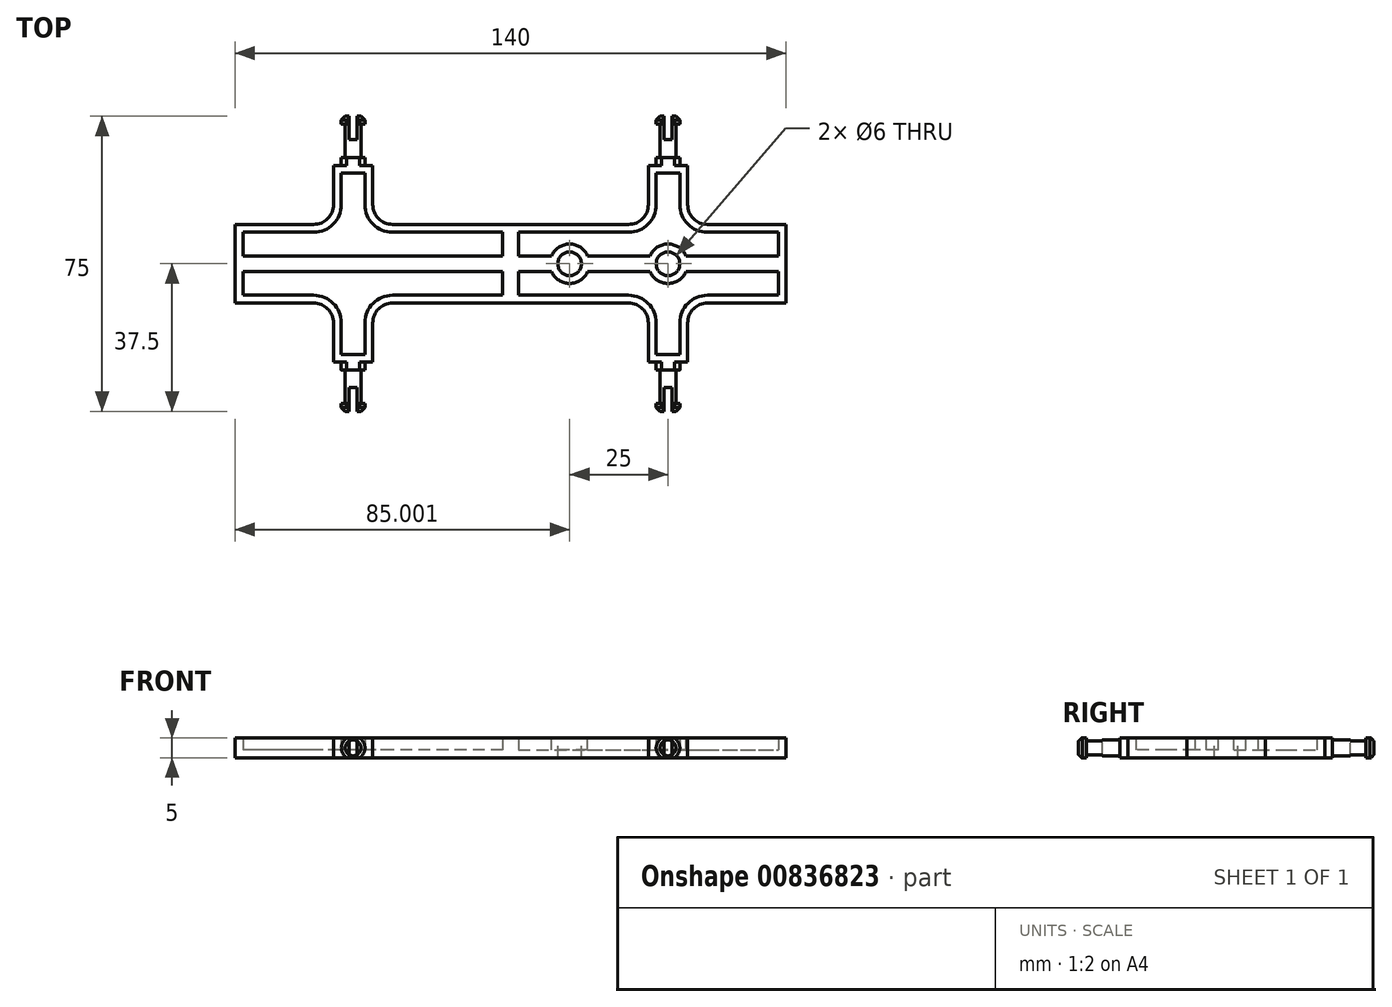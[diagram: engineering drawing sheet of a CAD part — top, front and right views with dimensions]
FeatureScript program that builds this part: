
annotation { "Feature Type Name" : "Feature", "Feature Type Description" : "" }
export const myFeature = defineFeature(function(context is Context, id is Id, definition is map)
    precondition{}
    {
        {
            var Q0;
            Q0=qCreatedBy(makeId("Front.planeOp"),FACE);
            var sketch = newSketch(context, id + "F0", { "sketchPlane" : qUnion([Q0])});
            skLineSegment(sketch, "E0.bottom", {"start": v(-42.85, 0) * mm, "end": v(27.15, 0) * mm});
            skLineSegment(sketch, "E0.top", {"start": v(-42.85, 10) * mm, "end": v(-12.85, 10) * mm});
            skLineSegment(sketch, "E0.left", {"start": v(-42.85, 0) * mm, "end": v(-42.85, 10) * mm});
            skLineSegment(sketch, "E0.right", {"start": v(27.15, 0) * mm, "end": v(27.15, 10) * mm});
            skLineSegment(sketch, "E1.top", {"start": v(-7.85, 25) * mm, "end": v(2.15, 25) * mm});
            skLineSegment(sketch, "E1.left", {"start": v(-7.85, 15) * mm, "end": v(-7.85, 25) * mm});
            skLineSegment(sketch, "E1.right", {"start": v(2.15, 15) * mm, "end": v(2.15, 25) * mm});
            skLineSegment(sketch, "E2.trimOffspring", {"start": v(7.15, 10) * mm, "end": v(27.15, 10) * mm});
            skPoint(sketch, "E3.visualSharp", {"position": v(-7.85, 10) * mm});
            skArc(sketch, "E3.filletArc", {"start": v(-12.85, 10) * mm, "mid": v(-9.31, 11.46) * mm, "end": v(-7.85, 15) * mm});
            skPoint(sketch, "E4.visualSharp", {"position": v(2.15, 10) * mm});
            skArc(sketch, "E4.filletArc", {"start": v(2.15, 15) * mm, "mid": v(3.62, 11.46) * mm, "end": v(7.15, 10) * mm});
            skSolve(sketch);
        }
        {
            var Q0;
            Q0=makeQuery(id+"F0.imprint","IMPRINT",FACE,{"disambiguationData":[TD([[makeQuery(id+"F0.imprint","IMPRINT",EDGE,{"derivedFrom":sQuery(id+"F0.wireOp",EDGE,"E0.bottom")}),1.0]])]});
            extrude(context, id + "F1", {"entities" : qUnion([Q0]), "endBound" : BoundingType.SYMMETRIC, "depth" : 5 * mm, "offsetDistance" : 25 * mm});
        }
        {
            var Q0;
            Q0=makeQuery(id+"F1.opExtrude","CAP_FACE",FACE,{"disambiguationData":[OSD([sQuery(id+"F0.wireOp",EDGE,"E0.bottom"),sQuery(id+"F0.wireOp",EDGE,"E0.top"),sQuery(id+"F0.wireOp",EDGE,"E0.left"),sQuery(id+"F0.wireOp",EDGE,"E0.right"),sQuery(id+"F0.wireOp",EDGE,"E1.top"),sQuery(id+"F0.wireOp",EDGE,"E1.left"),sQuery(id+"F0.wireOp",EDGE,"E1.right"),sQuery(id+"F0.wireOp",EDGE,"E2.trimOffspring"),sQuery(id+"F0.wireOp",EDGE,"E3.filletArc"),sQuery(id+"F0.wireOp",EDGE,"E4.filletArc")])],"isStart":false});
            shell(context, id + "F2", {"entities" : qUnion([Q0]), "thickness" : 2 * mm});
        }
        {
            var Q0;
            Q0=qCreatedBy(makeId("Front.planeOp"),FACE);
            var sketch = newSketch(context, id + "F3", { "sketchPlane" : qUnion([Q0])});
            skLineSegment(sketch, "E5", {"start": v(-5.85, 37.5) * mm, "end": v(-2.85, 37.5) * mm});
            skLineSegment(sketch, "E6", {"start": v(-2.85, 37.5) * mm, "end": v(-2.85, 25) * mm});
            skLineSegment(sketch, "E7", {"start": v(-2.85, 25) * mm, "end": v(-5.85, 25) * mm});
            skLineSegment(sketch, "E8", {"start": v(-5.85, 25) * mm, "end": v(-5.85, 27) * mm});
            skLineSegment(sketch, "E9", {"start": v(-5.85, 27) * mm, "end": v(-4.85, 27) * mm});
            skLineSegment(sketch, "E10", {"start": v(-4.85, 27) * mm, "end": v(-4.85, 35.5) * mm});
            skLineSegment(sketch, "E11", {"start": v(-4.85, 35.5) * mm, "end": v(-5.85, 35.5) * mm});
            skLineSegment(sketch, "E12", {"start": v(-5.85, 35.5) * mm, "end": v(-5.85, 37.5) * mm});
            skSolve(sketch);
        }
        {
            var Q0;
            Q0 = qSketchRegion(id + "F3", true);
            var Q1;
            Q1=sQuery(id+"F3.wireOp",EDGE,"E6");
            revolve(context, id + "F4", {"operationType" : NewBodyOperationType.ADD, "surfaceOperationType" : NewSurfaceOperationType.NEW, "entities" : qUnion([Q0]), "axis" : qUnion([Q1]), "revolveType" : RevolveType.FULL});
        }
        {
            var Q0;
            Q0=makeQuery(id+"F4.opRevolve","SWEPT_EDGE",EDGE,{"disambiguationData":[OSD([sQuery(id+"F3.wireOp",EDGE,"E5"),sQuery(id+"F3.wireOp",EDGE,"E12")])]});
            chamfer(context, id + "F5", {"entities" : qUnion([Q0]), "width" : 1 * mm, "tangentPropagation" : true});
        }
        {
            var Q0;
            Q0=makeQuery(id+"F4.opRevolve","SWEPT_FACE",FACE,{"disambiguationData":[OSD([sQuery(id+"F3.wireOp",EDGE,"E5")])]});
            var sketch = newSketch(context, id + "F6", { "sketchPlane" : qUnion([Q0])});
            skLineSegment(sketch, "E13.bottom", {"start": v(-55.26, 2.5) * mm, "end": v(46.37, 2.5) * mm});
            skLineSegment(sketch, "E13.top", {"start": v(-55.26, -2.5) * mm, "end": v(46.37, -2.5) * mm});
            skLineSegment(sketch, "E13.left", {"start": v(-55.26, 2.5) * mm, "end": v(-55.26, -2.5) * mm});
            skLineSegment(sketch, "E13.right", {"start": v(46.37, 2.5) * mm, "end": v(46.37, -2.5) * mm});
            skSolve(sketch);
        }
        {
            var Q0;
            Q0 = qSketchRegion(id + "F6", true);
            extrude(context, id + "F7", {"entities" : qUnion([Q0]), "operationType" : NewBodyOperationType.INTERSECT, "endBound" : BoundingType.THROUGH_ALL, "oppositeDirection" : true, "depth" : 25 * mm, "offsetDistance" : 25 * mm});
        }
        {
            var Q0;
            Q0=makeQuery(id+"F4.opRevolve","SWEPT_FACE",FACE,{"disambiguationData":[OSD([sQuery(id+"F3.wireOp",EDGE,"E5")])]});
            var sketch = newSketch(context, id + "F8", { "sketchPlane" : qUnion([Q0])});
            skLineSegment(sketch, "E14.bottom", {"start": v(-3.85, 6.1) * mm, "end": v(-1.85, 6.1) * mm});
            skLineSegment(sketch, "E14.top", {"start": v(-3.85, -6.84) * mm, "end": v(-1.85, -6.84) * mm});
            skLineSegment(sketch, "E14.left", {"start": v(-3.85, 6.1) * mm, "end": v(-3.85, -6.84) * mm});
            skLineSegment(sketch, "E14.right", {"start": v(-1.85, 6.1) * mm, "end": v(-1.85, -6.84) * mm});
            skSolve(sketch);
        }
        {
            var Q0;
            Q0 = qSketchRegion(id + "F8", true);
            extrude(context, id + "F9", {"entities" : qUnion([Q0]), "operationType" : NewBodyOperationType.REMOVE, "oppositeDirection" : true, "depth" : 6 * mm, "offsetDistance" : 25 * mm});
        }
        {
            var Q0;
            Q0=makeQuery(id+"F1.opExtrude","SWEPT_BODY",BODY,{"disambiguationData":[OSD([sQuery(id+"F0.wireOp",EDGE,"E0.bottom"),sQuery(id+"F0.wireOp",EDGE,"E0.top"),sQuery(id+"F0.wireOp",EDGE,"E0.left"),sQuery(id+"F0.wireOp",EDGE,"E0.right"),sQuery(id+"F0.wireOp",EDGE,"E1.top"),sQuery(id+"F0.wireOp",EDGE,"E1.left"),sQuery(id+"F0.wireOp",EDGE,"E1.right"),sQuery(id+"F0.wireOp",EDGE,"E2.trimOffspring"),sQuery(id+"F0.wireOp",EDGE,"E3.filletArc"),sQuery(id+"F0.wireOp",EDGE,"E4.filletArc")])]});
            var Q1;
            Q1=qCreatedBy(makeId("Top.planeOp"),FACE);
            mirror(context, id + "F10", {"operationType" : NewBodyOperationType.ADD, "entities" : qUnion([Q0]), "mirrorPlane" : qUnion([Q1])});
        }
        {
            var Q0;
            Q0=makeQuery(id+"F1.opExtrude","SWEPT_BODY",BODY,{"disambiguationData":[OSD([sQuery(id+"F0.wireOp",EDGE,"E0.bottom"),sQuery(id+"F0.wireOp",EDGE,"E0.top"),sQuery(id+"F0.wireOp",EDGE,"E0.left"),sQuery(id+"F0.wireOp",EDGE,"E0.right"),sQuery(id+"F0.wireOp",EDGE,"E1.top"),sQuery(id+"F0.wireOp",EDGE,"E1.left"),sQuery(id+"F0.wireOp",EDGE,"E1.right"),sQuery(id+"F0.wireOp",EDGE,"E2.trimOffspring"),sQuery(id+"F0.wireOp",EDGE,"E3.filletArc"),sQuery(id+"F0.wireOp",EDGE,"E4.filletArc")])]});
            var Q1;
            {var subQ0=makeQuery(id+"F1.opExtrude","SWEPT_FACE",FACE,{"disambiguationData":[OSD([sQuery(id+"F0.wireOp",EDGE,"E0.left")])]});Q1=makeQuery(id+"F10.boolean.opBoolean","MERGE",FACE,{"derivedFrom":[subQ0,makeQuery(id+"F10.opPattern","COPY",FACE,{"derivedFrom":subQ0,"instanceName":"1"})]});}
            mirror(context, id + "F11", {"operationType" : NewBodyOperationType.ADD, "entities" : qUnion([Q0]), "mirrorPlane" : qUnion([Q1])});
        }
        {
            var Q0;
            {var subQ0=makeQuery(id+"F7.boolean.opBoolean","MERGE",FACE,{"derivedFrom":[makeQuery(id+"F1.opExtrude","CAP_FACE",FACE,{"disambiguationData":[OSD([sQuery(id+"F0.wireOp",EDGE,"E0.bottom"),sQuery(id+"F0.wireOp",EDGE,"E0.top"),sQuery(id+"F0.wireOp",EDGE,"E0.left"),sQuery(id+"F0.wireOp",EDGE,"E0.right"),sQuery(id+"F0.wireOp",EDGE,"E1.top"),sQuery(id+"F0.wireOp",EDGE,"E1.left"),sQuery(id+"F0.wireOp",EDGE,"E1.right"),sQuery(id+"F0.wireOp",EDGE,"E2.trimOffspring"),sQuery(id+"F0.wireOp",EDGE,"E3.filletArc"),sQuery(id+"F0.wireOp",EDGE,"E4.filletArc")])],"isStart":false})],"fromTools":[makeQuery(id+"F7.boolean.toolComplement.opBoolean","COPY",FACE,{"derivedFrom":makeQuery(id+"F7.opExtrude","SWEPT_FACE",FACE,{"disambiguationData":[OSD([sQuery(id+"F6.wireOp",EDGE,"E13.top")])]})})]});var subQ1=makeQuery(id+"F10.boolean.opBoolean","MERGE",FACE,{"derivedFrom":[subQ0,makeQuery(id+"F10.opPattern","COPY",FACE,{"derivedFrom":subQ0,"instanceName":"1"})]});Q0=makeQuery(id+"F11.boolean.opBoolean","MERGE",FACE,{"derivedFrom":[subQ1,makeQuery(id+"F11.opPattern","COPY",FACE,{"derivedFrom":subQ1,"instanceName":"1"})]});}
            var sketch = newSketch(context, id + "F12", { "sketchPlane" : qUnion([Q0])});
            skCircle(sketch, "E15", {"center": v(-2.85, 0) * mm, "radius": 5 * mm});
            skCircle(sketch, "E16", {"center": v(-27.85, 0) * mm, "radius": 5 * mm});
            skSolve(sketch);
        }
        {
            var Q0;
            Q0 = qSketchRegion(id + "F12", true);
            extrude(context, id + "F13", {"entities" : qUnion([Q0]), "operationType" : NewBodyOperationType.ADD, "endBound" : BoundingType.UP_TO_NEXT, "oppositeDirection" : true, "depth" : 25 * mm, "offsetDistance" : 25 * mm});
        }
        {
            var Q0;
            {var subQ0=makeQuery(id+"F7.boolean.opBoolean","MERGE",FACE,{"derivedFrom":[makeQuery(id+"F1.opExtrude","CAP_FACE",FACE,{"disambiguationData":[OSD([sQuery(id+"F0.wireOp",EDGE,"E0.bottom"),sQuery(id+"F0.wireOp",EDGE,"E0.top"),sQuery(id+"F0.wireOp",EDGE,"E0.left"),sQuery(id+"F0.wireOp",EDGE,"E0.right"),sQuery(id+"F0.wireOp",EDGE,"E1.top"),sQuery(id+"F0.wireOp",EDGE,"E1.left"),sQuery(id+"F0.wireOp",EDGE,"E1.right"),sQuery(id+"F0.wireOp",EDGE,"E2.trimOffspring"),sQuery(id+"F0.wireOp",EDGE,"E3.filletArc"),sQuery(id+"F0.wireOp",EDGE,"E4.filletArc")])],"isStart":false})],"fromTools":[makeQuery(id+"F7.boolean.toolComplement.opBoolean","COPY",FACE,{"derivedFrom":makeQuery(id+"F7.opExtrude","SWEPT_FACE",FACE,{"disambiguationData":[OSD([sQuery(id+"F6.wireOp",EDGE,"E13.top")])]})})]});var subQ1=makeQuery(id+"F10.boolean.opBoolean","MERGE",FACE,{"derivedFrom":[subQ0,makeQuery(id+"F10.opPattern","COPY",FACE,{"derivedFrom":subQ0,"instanceName":"1"})]});Q0=makeQuery(id+"F13.boolean.opBoolean","MERGE",FACE,{"derivedFrom":[makeQuery(id+"F11.boolean.opBoolean","MERGE",FACE,{"derivedFrom":[subQ1,makeQuery(id+"F11.opPattern","COPY",FACE,{"derivedFrom":subQ1,"instanceName":"1"})]}),makeQuery(id+"F13.opExtrude","CAP_FACE",FACE,{"disambiguationData":[OSD([sQuery(id+"F12.wireOp",EDGE,"E15")])],"isStart":true}),makeQuery(id+"F13.opExtrude","CAP_FACE",FACE,{"disambiguationData":[OSD([sQuery(id+"F12.wireOp",EDGE,"E16")])],"isStart":true})]});}
            var sketch = newSketch(context, id + "F14", { "sketchPlane" : qUnion([Q0])});
            skPoint(sketch, "E17", {"position": v(-27.85, 0) * mm});
            skPoint(sketch, "E18", {"position": v(-2.85, 0) * mm});
            skSolve(sketch);
        }
        {
            var Q0;
            Q0=sQuery(id+"F14.wireOp",VERTEX,"E17");
            var Q1;
            Q1=sQuery(id+"F14.wireOp",VERTEX,"E18");
            var Q2;
            Q2=makeQuery(id+"F1.opExtrude","SWEPT_BODY",BODY,{"disambiguationData":[OSD([sQuery(id+"F0.wireOp",EDGE,"E0.bottom"),sQuery(id+"F0.wireOp",EDGE,"E0.top"),sQuery(id+"F0.wireOp",EDGE,"E0.left"),sQuery(id+"F0.wireOp",EDGE,"E0.right"),sQuery(id+"F0.wireOp",EDGE,"E1.top"),sQuery(id+"F0.wireOp",EDGE,"E1.left"),sQuery(id+"F0.wireOp",EDGE,"E1.right"),sQuery(id+"F0.wireOp",EDGE,"E2.trimOffspring"),sQuery(id+"F0.wireOp",EDGE,"E3.filletArc"),sQuery(id+"F0.wireOp",EDGE,"E4.filletArc")])]});
            hole(context, id + "F15", {"style" : HoleStyle.SIMPLE, "endStyle" : HoleEndStyle.THROUGH, "holeDiameter" : 6 * mm, "majorDiameter" : 5 * mm, "isTappedThrough" : true, "tappedDepth" : 12 * mm, "tapClearance" : 3, "locations" : qUnion([Q0, Q1]), "scope" : qUnion([Q2])});
        }
        {
            var Q0;
            Q0=makeQuery(id+"F1.opExtrude","SWEPT_BODY",BODY,{"disambiguationData":[OSD([sQuery(id+"F0.wireOp",EDGE,"E0.bottom"),sQuery(id+"F0.wireOp",EDGE,"E0.top"),sQuery(id+"F0.wireOp",EDGE,"E0.left"),sQuery(id+"F0.wireOp",EDGE,"E0.right"),sQuery(id+"F0.wireOp",EDGE,"E1.top"),sQuery(id+"F0.wireOp",EDGE,"E1.left"),sQuery(id+"F0.wireOp",EDGE,"E1.right"),sQuery(id+"F0.wireOp",EDGE,"E2.trimOffspring"),sQuery(id+"F0.wireOp",EDGE,"E3.filletArc"),sQuery(id+"F0.wireOp",EDGE,"E4.filletArc")])]});
            var Q1;
            Q1=qCreatedBy(makeId("Right.planeOp"),FACE);
            transform(context, id + "F16", {"entities" : qUnion([Q0]), "transformType" : TransformType.TRANSLATION_DISTANCE, "transformDirection" : qUnion([Q1]), "distance" : 40 * mm, "makeCopy" : false});
        }
        {
            var Q0;
            Q0=makeQuery(id+"F1.opExtrude","SWEPT_BODY",BODY,{"disambiguationData":[OSD([sQuery(id+"F0.wireOp",EDGE,"E0.bottom"),sQuery(id+"F0.wireOp",EDGE,"E0.top"),sQuery(id+"F0.wireOp",EDGE,"E0.left"),sQuery(id+"F0.wireOp",EDGE,"E0.right"),sQuery(id+"F0.wireOp",EDGE,"E1.top"),sQuery(id+"F0.wireOp",EDGE,"E1.left"),sQuery(id+"F0.wireOp",EDGE,"E1.right"),sQuery(id+"F0.wireOp",EDGE,"E2.trimOffspring"),sQuery(id+"F0.wireOp",EDGE,"E3.filletArc"),sQuery(id+"F0.wireOp",EDGE,"E4.filletArc")])]});
            var Q1;
            Q1=qCreatedBy(makeId("Right.planeOp"),FACE);
            transform(context, id + "F17", {"entities" : qUnion([Q0]), "transformType" : TransformType.TRANSLATION_DISTANCE, "transformDirection" : qUnion([Q1]), "distance" : 5 * mm, "makeCopy" : false});
        }
        {
            var Q0;
            Q0=makeQuery(id+"F1.opExtrude","SWEPT_BODY",BODY,{"disambiguationData":[OSD([sQuery(id+"F0.wireOp",EDGE,"E0.bottom"),sQuery(id+"F0.wireOp",EDGE,"E0.top"),sQuery(id+"F0.wireOp",EDGE,"E0.left"),sQuery(id+"F0.wireOp",EDGE,"E0.right"),sQuery(id+"F0.wireOp",EDGE,"E1.top"),sQuery(id+"F0.wireOp",EDGE,"E1.left"),sQuery(id+"F0.wireOp",EDGE,"E1.right"),sQuery(id+"F0.wireOp",EDGE,"E2.trimOffspring"),sQuery(id+"F0.wireOp",EDGE,"E3.filletArc"),sQuery(id+"F0.wireOp",EDGE,"E4.filletArc")])]});
            var Q1;
            Q1=qCreatedBy(makeId("Right.planeOp"),FACE);
            transform(context, id + "F18", {"entities" : qUnion([Q0]), "transformType" : TransformType.TRANSLATION_DISTANCE, "transformDirection" : qUnion([Q1]), "distance" : 2.5 * mm, "oppositeDirection" : true, "makeCopy" : false});
        }
        {
            var Q0;
            Q0=makeQuery(id+"F1.opExtrude","SWEPT_BODY",BODY,{"disambiguationData":[OSD([sQuery(id+"F0.wireOp",EDGE,"E0.bottom"),sQuery(id+"F0.wireOp",EDGE,"E0.top"),sQuery(id+"F0.wireOp",EDGE,"E0.left"),sQuery(id+"F0.wireOp",EDGE,"E0.right"),sQuery(id+"F0.wireOp",EDGE,"E1.top"),sQuery(id+"F0.wireOp",EDGE,"E1.left"),sQuery(id+"F0.wireOp",EDGE,"E1.right"),sQuery(id+"F0.wireOp",EDGE,"E2.trimOffspring"),sQuery(id+"F0.wireOp",EDGE,"E3.filletArc"),sQuery(id+"F0.wireOp",EDGE,"E4.filletArc")])]});
            var Q1;
            Q1=makeQuery(id+"F1.opExtrude","CAP_EDGE",EDGE,{"disambiguationData":[OSD([sQuery(id+"F0.wireOp",EDGE,"E2.trimOffspring")])],"isStart":true});
            transform(context, id + "F19", {"entities" : qUnion([Q0]), "transformType" : TransformType.ROTATION, "transformAxis" : qUnion([Q1]), "angle" : 90 * degree, "makeCopy" : false});
        }
        {
            var Q0;
            Q0=makeQuery(id+"F1.opExtrude","SWEPT_BODY",BODY,{"disambiguationData":[OSD([sQuery(id+"F0.wireOp",EDGE,"E0.bottom"),sQuery(id+"F0.wireOp",EDGE,"E0.top"),sQuery(id+"F0.wireOp",EDGE,"E0.left"),sQuery(id+"F0.wireOp",EDGE,"E0.right"),sQuery(id+"F0.wireOp",EDGE,"E1.top"),sQuery(id+"F0.wireOp",EDGE,"E1.left"),sQuery(id+"F0.wireOp",EDGE,"E1.right"),sQuery(id+"F0.wireOp",EDGE,"E2.trimOffspring"),sQuery(id+"F0.wireOp",EDGE,"E3.filletArc"),sQuery(id+"F0.wireOp",EDGE,"E4.filletArc")])]});
            transform(context, id + "F20", {"entities" : qUnion([Q0]), "transformType" : TransformType.TRANSLATION_3D, "dx" : 0 * mm, "dy" : 0 * mm, "dz" : -7.5 * mm, "makeCopy" : false});
        }
        {
            var Q0;
            Q0=makeQuery(id+"F1.opExtrude","SWEPT_BODY",BODY,{"disambiguationData":[OSD([sQuery(id+"F0.wireOp",EDGE,"E0.bottom"),sQuery(id+"F0.wireOp",EDGE,"E0.top"),sQuery(id+"F0.wireOp",EDGE,"E0.left"),sQuery(id+"F0.wireOp",EDGE,"E0.right"),sQuery(id+"F0.wireOp",EDGE,"E1.top"),sQuery(id+"F0.wireOp",EDGE,"E1.left"),sQuery(id+"F0.wireOp",EDGE,"E1.right"),sQuery(id+"F0.wireOp",EDGE,"E2.trimOffspring"),sQuery(id+"F0.wireOp",EDGE,"E3.filletArc"),sQuery(id+"F0.wireOp",EDGE,"E4.filletArc")])]});
            var Q1;
            Q1=makeQuery(id+"F11.opPattern","COPY",EDGE,{"derivedFrom":makeQuery(id+"F1.opExtrude","CAP_EDGE",EDGE,{"disambiguationData":[OSD([sQuery(id+"F0.wireOp",EDGE,"E2.trimOffspring")])],"isStart":false}),"instanceName":"1"});
            transform(context, id + "F21", {"entities" : qUnion([Q0]), "transformType" : TransformType.ROTATION, "transformAxis" : qUnion([Q1]), "angle" : 180 * degree, "makeCopy" : false});
        }
        {
            var Q0;
            Q0=makeQuery(id+"F1.opExtrude","SWEPT_BODY",BODY,{"disambiguationData":[OSD([sQuery(id+"F0.wireOp",EDGE,"E0.bottom"),sQuery(id+"F0.wireOp",EDGE,"E0.top"),sQuery(id+"F0.wireOp",EDGE,"E0.left"),sQuery(id+"F0.wireOp",EDGE,"E0.right"),sQuery(id+"F0.wireOp",EDGE,"E1.top"),sQuery(id+"F0.wireOp",EDGE,"E1.left"),sQuery(id+"F0.wireOp",EDGE,"E1.right"),sQuery(id+"F0.wireOp",EDGE,"E2.trimOffspring"),sQuery(id+"F0.wireOp",EDGE,"E3.filletArc"),sQuery(id+"F0.wireOp",EDGE,"E4.filletArc")])]});
            transform(context, id + "F22", {"entities" : qUnion([Q0]), "transformType" : TransformType.TRANSLATION_3D, "dx" : 0 * mm, "dy" : 0 * mm, "dz" : 5 * mm, "makeCopy" : false});
        }
    });
